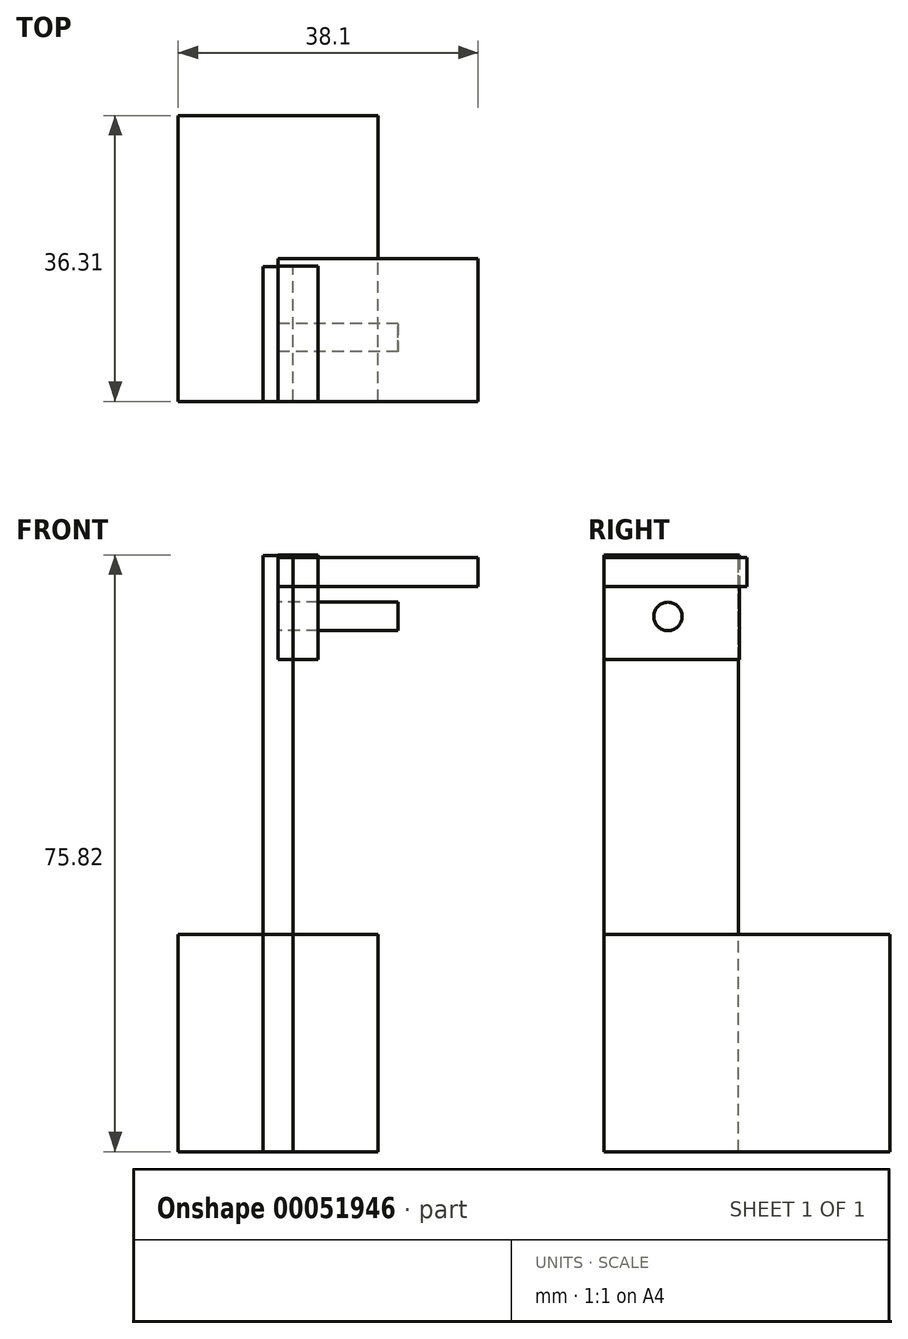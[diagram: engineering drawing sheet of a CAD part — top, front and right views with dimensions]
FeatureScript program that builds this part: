
annotation { "Feature Type Name" : "Feature", "Feature Type Description" : "" }
export const myFeature = defineFeature(function(context is Context, id is Id, definition is map)
    precondition{}
    {
        {
            var Q0;
            Q0=qCreatedBy(makeId("Right.planeOp"),FACE);
            var sketch = newSketch(context, id + "F0", { "sketchPlane" : qUnion([Q0])});
            skLineSegment(sketch, "E0.bottom", {"start": v(0, 0) * mm, "end": v(36.3, 0) * mm});
            skLineSegment(sketch, "E0.top", {"start": v(0, 27.58) * mm, "end": v(36.3, 27.58) * mm});
            skLineSegment(sketch, "E0.left", {"start": v(0, 0) * mm, "end": v(0, 27.58) * mm});
            skLineSegment(sketch, "E0.right", {"start": v(36.3, 0) * mm, "end": v(36.3, 27.58) * mm});
            skSolve(sketch);
        }
        {
            var Q0;
            Q0=qCreatedBy(makeId("Right.planeOp"),FACE);
            var sketch = newSketch(context, id + "F1", { "sketchPlane" : qUnion([Q0])});
            skLineSegment(sketch, "E1.bottom", {"start": v(0, 0) * mm, "end": v(17.1, 0) * mm});
            skLineSegment(sketch, "E1.top", {"start": v(0, 75.76) * mm, "end": v(17.1, 75.76) * mm});
            skLineSegment(sketch, "E1.left", {"start": v(0, 0) * mm, "end": v(0, 75.76) * mm});
            skLineSegment(sketch, "E1.right", {"start": v(17.1, 0) * mm, "end": v(17.1, 75.76) * mm});
            skSolve(sketch);
        }
        {
            var Q0;
            Q0=qCreatedBy(makeId("Right.planeOp"),FACE);
            var sketch = newSketch(context, id + "F2", { "sketchPlane" : qUnion([Q0])});
            skLineSegment(sketch, "E2.bottom", {"start": v(0, 75.46) * mm, "end": v(18.11, 75.46) * mm});
            skLineSegment(sketch, "E2.top", {"start": v(0, 71.82) * mm, "end": v(18.11, 71.82) * mm});
            skLineSegment(sketch, "E2.left", {"start": v(0, 75.46) * mm, "end": v(0, 71.82) * mm});
            skLineSegment(sketch, "E2.right", {"start": v(18.11, 75.46) * mm, "end": v(18.11, 71.82) * mm});
            skSolve(sketch);
        }
        {
            var Q0;
            Q0=qCreatedBy(makeId("Right.planeOp"),FACE);
            var sketch = newSketch(context, id + "F3", { "sketchPlane" : qUnion([Q0])});
            skLineSegment(sketch, "E3.bottom", {"start": v(0, 75.82) * mm, "end": v(17.2, 75.82) * mm});
            skLineSegment(sketch, "E3.top", {"start": v(0, 62.53) * mm, "end": v(17.2, 62.53) * mm});
            skLineSegment(sketch, "E3.left", {"start": v(0, 75.82) * mm, "end": v(0, 62.53) * mm});
            skLineSegment(sketch, "E3.right", {"start": v(17.2, 75.82) * mm, "end": v(17.2, 62.53) * mm});
            skSolve(sketch);
        }
        {
            var Q0;
            Q0=qCreatedBy(makeId("Right.planeOp"),FACE);
            var sketch = newSketch(context, id + "F4", { "sketchPlane" : qUnion([Q0])});
            skCircle(sketch, "E4", {"center": v(8.1, 68) * mm, "radius": 1.8 * mm});
            skSolve(sketch);
        }
        {
            var Q0;
            Q0=makeQuery(id+"F0.imprint","IMPRINT",FACE,{"disambiguationData":[TD([[makeQuery(id+"F0.imprint","IMPRINT",EDGE,{"derivedFrom":sQuery(id+"F0.wireOp",EDGE,"E0.bottom")}),1.0]])]});
            extrude(context, id + "F5", {"entities" : qUnion([Q0]), "endBound" : BoundingType.SYMMETRIC, "depth" : 25.4 * mm});
        }
        {
            var Q0;
            Q0=makeQuery(id+"F3.imprint","IMPRINT",FACE,{"disambiguationData":[TD([[makeQuery(id+"F3.imprint","IMPRINT",EDGE,{"derivedFrom":sQuery(id+"F3.wireOp",EDGE,"E3.bottom")}),-1.0]])]});
            extrude(context, id + "F6", {"entities" : qUnion([Q0]), "depth" : 5.08 * mm});
        }
        {
            var Q0;
            Q0=makeQuery(id+"F1.imprint","IMPRINT",FACE,{"disambiguationData":[TD([[makeQuery(id+"F1.imprint","IMPRINT",EDGE,{"derivedFrom":sQuery(id+"F1.wireOp",EDGE,"E1.bottom")}),1.0]])]});
            extrude(context, id + "F7", {"entities" : qUnion([Q0]), "endBound" : BoundingType.SYMMETRIC, "depth" : 3.8 * mm});
        }
        {
            var Q0;
            Q0 = qSketchRegion(id + "F4", true);
            extrude(context, id + "F8", {"entities" : qUnion([Q0]), "depth" : 15.24 * mm});
        }
        {
            var Q0;
            Q0 = qSketchRegion(id + "F2", true);
            extrude(context, id + "F9", {"entities" : qUnion([Q0]), "depth" : 25.4 * mm});
        }
    });
